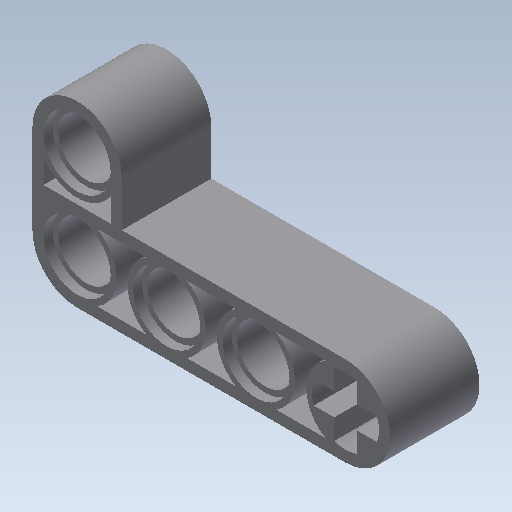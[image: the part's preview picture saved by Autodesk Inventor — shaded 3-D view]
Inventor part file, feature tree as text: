
AUTODESK INVENTOR PART (.ipt)
format: ipt  version: 2020 (Build 240168000, 168)  size: 260,608 bytes
history: native  units: mm
features: extrude x6, sketch x6
ambient origin geometry x8: Origin, YZ Plane, XZ Plane, XY Plane, X Axis, Y Axis, Z Axis, Center Point
bodies: Solid1 (feature_tree)
feature tree (12):
  extrude  "Extrusion1"  Depth=4.0mm
  extrude  "Extrusion13"  Depth=4.0mm
  extrude  "Extrusion14"  TaperAngle=0.0deg  [1 undecoded]
  extrude  "Extrusion15"  Depth=4.0mm
  extrude  "Extrusion16"  Depth=12.0mm
  extrude  "Extrusion17"  Depth=7.0mm
  sketch  "Sketch1"  dims[d3=4.0mm d4=4.0mm]
  sketch  "Sketch13"  dims[d5=4.0mm d6=24.0mm]
  sketch  "Sketch14"  dims[d7=8.0mm d10=0.0mm]
  sketch  "Sketch15"  dims[d12=90.0deg d14=4.0mm]
  sketch  "Sketch16"  dims[d15=4.0mm d16=12.0mm]
  sketch  "Sketch17"  dims[d17=8.0mm d18=0.0mm d69=7.0mm d123=12.0mm d124=6.0mm d125=3.0mm d126=3.0mm d127=3.0mm d128=3.0mm d129=2.0mm d130=2.0mm d131=2.0mm d132=2.0mm d133=1.0mm d134=1.0mm d135=1.0mm d136=1.0mm d137=10.0mm d138=0.0mm d139=5.0mm d140=5.0mm d141=10.0mm d143=10.0mm d144=30.0mm d146=8.0mm d148=10.0mm d149=0.0mm d150=6.0mm d151=6.0mm d152=6.0mm d153=6.0mm d154=0.8mm d155=0.0mm d156=6.0mm d157=6.0mm d158=6.0mm d159=6.0mm d160=0.8mm d161=0.0mm d162=7.0mm d163=7.0mm d164=7.0mm d165=6.0mm d166=4.0mm d167=10.0mm d169=10.0mm d170=30.0mm d172=8.0mm d174=0.8mm d175=0.0mm]
note: 1 required parameter value undecoded (feature->parameter linkage not recoverable at this tier; creation-order binding heuristic only, values carry confidence <= 0.55)
